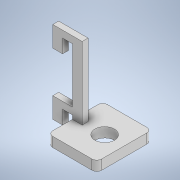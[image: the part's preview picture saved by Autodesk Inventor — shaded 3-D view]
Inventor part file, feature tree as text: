
AUTODESK INVENTOR PART (.ipt)
format: ipt  version: 2020.2 (Build 242310000, 310)  size: 158,720 bytes
history: native  units: in
note: dims shown in document units (in); Inventor stores cm internally (conversion verified against a paired STEP export)
features: extrude x3, sketch x3, fillet x1
ambient origin geometry x8: Origin, YZ Plane, XZ Plane, XY Plane, X Axis, Y Axis, Z Axis, Center Point
bodies: Solid1 (feature_tree)
feature tree (7):
  extrude  "Extrusion1"  Depth=0.175in
  extrude  "Extrusion4"  Depth=0.25in
  extrude  "Extrusion5"  Depth=0.25in
  fillet  "Fillet2"  Radius=0.15in
  sketch  "Sketch1"  dims[d1=1.4in d2=0.175in]
  sketch  "Sketch4"  dims[d3=0.175in d4=0.25in]
  sketch  "Sketch5"  dims[d6=0.25in d7=0.25in d11=0.15in d12=0.0in d13=0.525in d14=0.525in d23=1.25in d24=0.25in d25=1.4in d26=0.0in d27=0.5in d28=1.85in d29=0.0in d30=0.125in]
